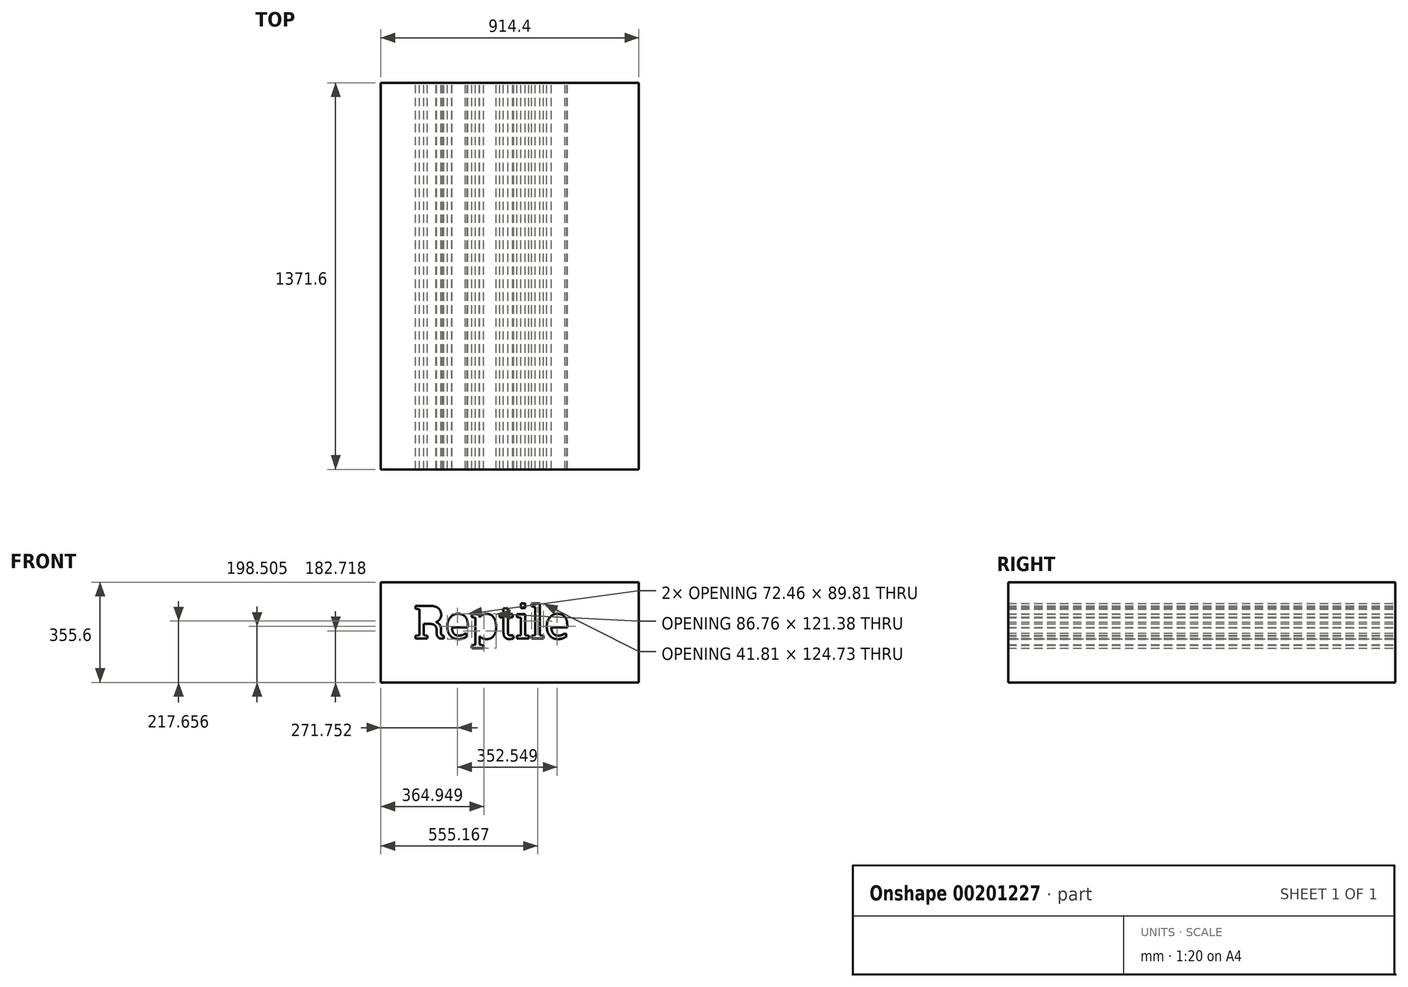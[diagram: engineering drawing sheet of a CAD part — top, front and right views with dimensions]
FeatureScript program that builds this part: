
annotation { "Feature Type Name" : "Feature", "Feature Type Description" : "" }
export const myFeature = defineFeature(function(context is Context, id is Id, definition is map)
    precondition{}
    {
        {
            var Q0;
            Q0=qCreatedBy(makeId("Front.planeOp"),FACE);
            var sketch = newSketch(context, id + "F0", { "sketchPlane" : qUnion([Q0])});
            skLineSegment(sketch, "E0.bottom", {"start": v(-505.82, 117.01) * mm, "end": v(408.58, 117.01) * mm});
            skLineSegment(sketch, "E0.top", {"start": v(-505.82, -238.59) * mm, "end": v(408.58, -238.59) * mm});
            skLineSegment(sketch, "E0.left", {"start": v(-505.82, 117.01) * mm, "end": v(-505.82, -238.59) * mm});
            skLineSegment(sketch, "E0.right", {"start": v(408.58, 117.01) * mm, "end": v(408.58, -238.59) * mm});
            skText(sketch, "E1", { "text": "Reptile", "fontName": "RobotoSlab-Regular.ttf"});
            const initialGuessF0  = {"E1": [-0.3883, -0.0833, 1, 0, 0.1179]};
            skSetInitialGuess(sketch, initialGuessF0);
            skSolve(sketch);
        }
        {
            var Q0;
            Q0 = qSketchRegion(id + "F0", true);
            extrude(context, id + "F1", {"entities" : qUnion([Q0]), "depth" : 1371.6 * mm});
        }
    });
